annotation { "Feature Type Name" : "Feature", "Feature Type Description" : "" }
export const myFeature = defineFeature(function(context is Context, id is Id, definition is map)
    precondition{}
    {
        {
            var Q0;
            Q0=qCreatedBy(makeId("Top.planeOp"),FACE);
            var sketch = newSketch(context, id + "F0", { "sketchPlane" : qUnion([Q0])});
            skLineSegment(sketch, "E0", {"start": v(0, 0) * mm, "end": v(0, 609.6) * mm});
            skLineSegment(sketch, "E1", {"start": v(0, 609.6) * mm, "end": v(2743.2, 3534.73) * mm});
            skLineSegment(sketch, "E2", {"start": v(2743.2, 3534.73) * mm, "end": v(8839.2, 5486.4) * mm});
            skLineSegment(sketch, "E3", {"start": v(8839.2, 5486.4) * mm, "end": v(13696.12, 3681.04) * mm});
            skLineSegment(sketch, "E4", {"start": v(13696.12, 3681.04) * mm, "end": v(15849.6, 1524) * mm});
            skLineSegment(sketch, "E5", {"start": v(15849.6, 1524) * mm, "end": v(15849.6, 0) * mm});
            skLineSegment(sketch, "E6", {"start": v(0, 0) * mm, "end": v(15849.6, 0) * mm});
            skLineSegment(sketch, "E7", {"start": v(8839.2, 5486.4) * mm, "end": v(8839.2, 0) * mm, "construction": true});
            skLineSegment(sketch, "E8.bottom", {"start": v(13696.12, 2438.4) * mm, "end": v(5181.6, 2438.4) * mm, "construction": true});
            skLineSegment(sketch, "E8.top", {"start": v(13696.12, 0) * mm, "end": v(5181.6, 0) * mm});
            skLineSegment(sketch, "E8.left", {"start": v(13696.12, 2438.4) * mm, "end": v(13696.12, 0) * mm, "construction": true});
            skLineSegment(sketch, "E8.right", {"start": v(5181.6, 2438.4) * mm, "end": v(5181.6, 0) * mm, "construction": true});
            skLineSegment(sketch, "E9.bottom", {"start": v(0, 0) * mm, "end": v(1524, 0) * mm});
            skLineSegment(sketch, "E9.top", {"start": v(0, 609.6) * mm, "end": v(1524, 609.6) * mm});
            skLineSegment(sketch, "E9.right", {"start": v(1524, 0) * mm, "end": v(1524, 609.6) * mm});
            skSolve(sketch);
        }
        {
            var Q0;
            Q0=qCreatedBy(makeId("Top.planeOp"),FACE);
            var sketch = newSketch(context, id + "F1", { "sketchPlane" : qUnion([Q0])});
            skCircle(sketch, "E10", {"center": v(1828.8, 762) * mm, "radius": 45.72 * mm});
            skCircle(sketch, "E11", {"center": v(0, 609.6) * mm, "radius": 45.72 * mm});
            skCircle(sketch, "E12", {"center": v(5181.6, 2438.4) * mm, "radius": 45.72 * mm});
            skCircle(sketch, "E13", {"center": v(7924.8, 0) * mm, "radius": 45.72 * mm});
            skPoint(sketch, "E14.0", {"position": v(13696.12, 2438.4) * mm});
            skLineSegment(sketch, "E15.0", {"start": v(13696.12, 2438.4) * mm, "end": v(13696.12, 0) * mm});
            skCircle(sketch, "E16", {"center": v(13696.12, 3048) * mm, "radius": 45.72 * mm});
            skPoint(sketch, "E17.0", {"position": v(8839.2, 5486.4) * mm});
            skPoint(sketch, "E18.0", {"position": v(13696.12, 3681.04) * mm});
            skPoint(sketch, "E19.0", {"position": v(2743.2, 3534.73) * mm});
            skCircle(sketch, "E20", {"center": v(8839.2, 5486.4) * mm, "radius": 15.24 * mm});
            skCircle(sketch, "E21", {"center": v(2743.2, 3534.73) * mm, "radius": 15.24 * mm});
            skCircle(sketch, "E22", {"center": v(13696.12, 3681.04) * mm, "radius": 15.24 * mm});
            skLineSegment(sketch, "E23", {"start": v(13696.12, 2438.4) * mm, "end": v(13696.12, 3264.57) * mm, "construction": true});
            skSolve(sketch);
        }
        {
            var Q0;
            Q0=makeQuery(id+"F1.imprint","IMPRINT",FACE,{"disambiguationData":[TD([[makeQuery(id+"F1.imprint","IMPRINT",EDGE,{"derivedFrom":sQuery(id+"F1.wireOp",EDGE,"E11")}),1.0]])]});
            extrude(context, id + "F2", {"entities" : qUnion([Q0]), "depth" : 152.4 * mm, "offsetDistance" : 30.48 * mm});
        }
        {
            var Q0;
            Q0=makeQuery(id+"F1.imprint","IMPRINT",FACE,{"disambiguationData":[TD([[makeQuery(id+"F1.imprint","IMPRINT",EDGE,{"derivedFrom":sQuery(id+"F1.wireOp",EDGE,"E12")}),1.0]])]});
            extrude(context, id + "F3", {"entities" : qUnion([Q0]), "depth" : 2438.4 * mm, "offsetDistance" : 30.48 * mm});
        }
        {
            var Q0;
            Q0=makeQuery(id+"F1.imprint","IMPRINT",FACE,{"disambiguationData":[TD([[makeQuery(id+"F1.imprint","IMPRINT",EDGE,{"derivedFrom":sQuery(id+"F1.wireOp",EDGE,"E13")}),1.0]])]});
            extrude(context, id + "F4", {"entities" : qUnion([Q0]), "depth" : 6096 * mm, "offsetDistance" : 30.48 * mm});
        }
        {
            var Q0;
            Q0=makeQuery(id+"F1.imprint","IMPRINT",FACE,{"disambiguationData":[TD([[makeQuery(id+"F1.imprint","IMPRINT",EDGE,{"derivedFrom":sQuery(id+"F1.wireOp",EDGE,"E16")}),1.0]])]});
            var Q1;
            Q1=sQuery(id+"F1.wireOp",EDGE,"E16");
            extrude(context, id + "F5", {"entities" : qUnion([Q0]), "surfaceEntities" : qUnion([Q1]), "depth" : 3657.6 * mm, "offsetDistance" : 30.48 * mm});
        }
        {
            var Q0;
            Q0=makeQuery(id+"F1.imprint","IMPRINT",FACE,{"disambiguationData":[TD([[makeQuery(id+"F1.imprint","IMPRINT",EDGE,{"derivedFrom":sQuery(id+"F1.wireOp",EDGE,"E10")}),1.0]])]});
            extrude(context, id + "F6", {"entities" : qUnion([Q0]), "depth" : 1219.2 * mm, "offsetDistance" : 30.48 * mm});
        }
        {
            var Q0;
            Q0=makeQuery(id+"F2.opExtrude","CAP_FACE",FACE,{"disambiguationData":[OSD([sQuery(id+"F1.wireOp",EDGE,"E11")])],"isStart":false});
            var sketch = newSketch(context, id + "F7", { "sketchPlane" : qUnion([Q0])});
            skPoint(sketch, "E24.0", {"position": v(0, 609.6) * mm});
            skSolve(sketch);
        }
        {
            var Q0;
            Q0=makeQuery(id+"F6.opExtrude","CAP_FACE",FACE,{"disambiguationData":[OSD([sQuery(id+"F1.wireOp",EDGE,"E10")])],"isStart":false});
            var sketch = newSketch(context, id + "F8", { "sketchPlane" : qUnion([Q0])});
            skPoint(sketch, "E25.0", {"position": v(1828.8, 762) * mm});
            skSolve(sketch);
        }
        {
            var Q0;
            Q0=makeQuery(id+"F3.opExtrude","CAP_FACE",FACE,{"disambiguationData":[OSD([sQuery(id+"F1.wireOp",EDGE,"E12")])],"isStart":false});
            var sketch = newSketch(context, id + "F9", { "sketchPlane" : qUnion([Q0])});
            skPoint(sketch, "E26.0", {"position": v(5181.6, 2438.4) * mm});
            skSolve(sketch);
        }
        {
            var Q0;
            Q0=makeQuery(id+"F4.opExtrude","CAP_FACE",FACE,{"disambiguationData":[OSD([sQuery(id+"F1.wireOp",EDGE,"E13")])],"isStart":false});
            var sketch = newSketch(context, id + "F10", { "sketchPlane" : qUnion([Q0])});
            skPoint(sketch, "E27.0", {"position": v(7924.8, 0) * mm});
            skSolve(sketch);
        }
        {
            var Q0;
            Q0=makeQuery(id+"F5.opExtrude","CAP_FACE",FACE,{"disambiguationData":[OSD([sQuery(id+"F1.wireOp",EDGE,"E16")])],"isStart":false});
            var sketch = newSketch(context, id + "F11", { "sketchPlane" : qUnion([Q0])});
            skPoint(sketch, "E28.0", {"position": v(13696.12, 3048) * mm});
            skSolve(sketch);
        }
        {
            var Q0;
            Q0=qCreatedBy(makeId("Front.planeOp"),FACE);
            var sketch = newSketch(context, id + "F12", { "sketchPlane" : qUnion([Q0])});
            skPoint(sketch, "E29.0", {"position": v(0, 152.4) * mm});
            skPoint(sketch, "E30.0", {"position": v(1828.8, 1219.2) * mm});
            skPoint(sketch, "E31.0", {"position": v(5181.6, 2438.4) * mm});
            skPoint(sketch, "E32.0", {"position": v(7924.8, 6096) * mm});
            skPoint(sketch, "E33.0", {"position": v(13696.12, 3657.6) * mm});
            skPoint(sketch, "E34.0", {"position": v(15849.6, 0) * mm});
            skLineSegment(sketch, "E35", {"start": v(0, 152.4) * mm, "end": v(1828.8, 1219.2) * mm});
            skLineSegment(sketch, "E36", {"start": v(1828.8, 1219.2) * mm, "end": v(5181.6, 2438.4) * mm});
            skLineSegment(sketch, "E37", {"start": v(5181.6, 2438.4) * mm, "end": v(7924.8, 6096) * mm});
            skLineSegment(sketch, "E38", {"start": v(7924.8, 6096) * mm, "end": v(13696.12, 3657.6) * mm});
            skLineSegment(sketch, "E39", {"start": v(13696.12, 3657.6) * mm, "end": v(15849.6, 0) * mm});
            skLineSegment(sketch, "E40", {"start": v(0, 152.4) * mm, "end": v(0, 0) * mm});
            skLineSegment(sketch, "E41", {"start": v(0, 0) * mm, "end": v(15849.6, 0) * mm});
            skSolve(sketch);
        }
        {
            var Q0;
            Q0=sQuery(id+"F12.wireOp",VERTEX,"E34.0");
            var Q1;
            Q1=sQuery(id+"F0.wireOp",EDGE,"E6");
            cPlane(context, id + "F13", {"entities" : qUnion([Q0, Q1]), "cplaneType" : CPlaneType.LINE_POINT, "offset" : 25.4 * mm, "width" : 152.4 * mm, "height" : 152.4 * mm});
        }
        {
            var Q0;
            Q0=sQuery(id+"F0.wireOp",VERTEX,"E8.top.start");
            var Q1;
            Q1=sQuery(id+"F0.wireOp",EDGE,"E8.top");
            cPlane(context, id + "F14", {"entities" : qUnion([Q0, Q1]), "cplaneType" : CPlaneType.LINE_POINT, "offset" : 25.4 * mm, "width" : 152.4 * mm, "height" : 152.4 * mm});
        }
        {
            var Q0;
            Q0=sQuery(id+"F0.wireOp",VERTEX,"E7.end");
            var Q1;
            Q1=sQuery(id+"F0.wireOp",EDGE,"E8.top");
            cPlane(context, id + "F15", {"entities" : qUnion([Q0, Q1]), "cplaneType" : CPlaneType.LINE_POINT, "offset" : 25.4 * mm, "width" : 152.4 * mm, "height" : 152.4 * mm});
        }
        {
            var Q0;
            Q0=sQuery(id+"F1.wireOp",VERTEX,"E13.center");
            var Q1;
            Q1=sQuery(id+"F0.wireOp",EDGE,"E8.top");
            cPlane(context, id + "F16", {"entities" : qUnion([Q0, Q1]), "cplaneType" : CPlaneType.LINE_POINT, "offset" : 25.4 * mm, "width" : 152.4 * mm, "height" : 152.4 * mm});
        }
        {
            var Q0;
            Q0=sQuery(id+"F0.wireOp",VERTEX,"E8.top.end");
            var Q1;
            Q1=sQuery(id+"F0.wireOp",EDGE,"E6");
            cPlane(context, id + "F17", {"entities" : qUnion([Q0, Q1]), "cplaneType" : CPlaneType.LINE_POINT, "offset" : 25.4 * mm, "width" : 152.4 * mm, "height" : 152.4 * mm});
        }
        {
            var Q0;
            Q0=sQuery(id+"F1.wireOp",VERTEX,"E10.center");
            var Q1;
            Q1=sQuery(id+"F0.wireOp",EDGE,"E9.top");
            cPlane(context, id + "F18", {"entities" : qUnion([Q0, Q1]), "cplaneType" : CPlaneType.LINE_POINT, "offset" : 25.4 * mm, "width" : 152.4 * mm, "height" : 152.4 * mm});
        }
        {
            var Q0;
            Q0=qCreatedBy(id+"F13.planeOp",FACE);
            var sketch = newSketch(context, id + "F19", { "sketchPlane" : qUnion([Q0])});
            skPoint(sketch, "E42.0", {"position": v(1524, 0) * mm});
            skPoint(sketch, "E43.0", {"position": v(0, 0) * mm});
            skLineSegment(sketch, "E44", {"start": v(0, 0) * mm, "end": v(1524, 0) * mm});
            skSolve(sketch);
        }
        {
            var Q0;
            Q0=qCreatedBy(id+"F14.planeOp",FACE);
            var sketch = newSketch(context, id + "F20", { "sketchPlane" : qUnion([Q0])});
            skPoint(sketch, "E45.0", {"position": v(0, 3657.6) * mm});
            skPoint(sketch, "E46.0", {"position": v(-3681.04, 0) * mm});
            skFitSpline(sketch, "E47", {"points": [v(0, 3657.6) * mm, v(-2829.93, 3657.6) * mm, v(-3266.02, 3355.39) * mm, v(-3455.52, 2857.54) * mm, v(-3466.42, 2011.87) * mm, v(-3681.04, 0) * mm], "startDerivative": vector(-11892.45, -467.18) * mm, "endDerivative": vector(-448.43, -6710.95) * mm});
            skSolve(sketch);
        }
        {
            var Q0;
            Q0=qCreatedBy(id+"F15.planeOp",FACE);
            var sketch = newSketch(context, id + "F21", { "sketchPlane" : qUnion([Q0])});
            skPoint(sketch, "E48.0", {"position": v(-5486.4, 0) * mm});
            skPoint(sketch, "E49.0", {"position": v(-3048, 3657.6) * mm});
            skPoint(sketch, "E50", {"position": v(0, 5709.66) * mm});
            skFitSpline(sketch, "E51", {"points": [v(0, 5709.66) * mm, v(-1542.44, 4811.64) * mm, v(-3048, 3657.6) * mm, v(-5486.4, 0) * mm], "startDerivative": vector(-5647.14, -3250.63) * mm, "endDerivative": vector(-5724.6, -9712.29) * mm});
            skSolve(sketch);
        }
        {
            var Q0;
            Q0=qCreatedBy(id+"F16.planeOp",FACE);
            var sketch = newSketch(context, id + "F22", { "sketchPlane" : qUnion([Q0])});
            skPoint(sketch, "E52.0", {"position": v(0, 6096) * mm});
            skPoint(sketch, "E53", {"position": v(-5193.65, 0) * mm});
            skFitSpline(sketch, "E54", {"points": [v(0, 6096) * mm, v(-1926, 4551.62) * mm, v(-3350.94, 3287.9) * mm, v(-4609.72, 1384.51) * mm, v(-5193.65, 0) * mm], "startDerivative": vector(-7241.61, -5856.52) * mm, "endDerivative": vector(-2275.9, -6106.6) * mm});
            skSolve(sketch);
        }
        {
            var Q0;
            Q0=qCreatedBy(id+"F17.planeOp",FACE);
            var sketch = newSketch(context, id + "F23", { "sketchPlane" : qUnion([Q0])});
            skPoint(sketch, "E55.0", {"position": v(2438.4, 2438.4) * mm});
            skPoint(sketch, "E56.0", {"position": v(0, 2438.4) * mm});
            skPoint(sketch, "E57", {"position": v(4315.4, 0) * mm});
            skFitSpline(sketch, "E58", {"points": [v(0, 2438.4) * mm, v(1379.95, 2438.4) * mm, v(2438.4, 2438.4) * mm, v(3673.67, 1296.18) * mm, v(4315.4, 0) * mm], "startDerivative": vector(8349.63, -169.14) * mm, "endDerivative": vector(2877.01, -3268.1) * mm});
            skSolve(sketch);
        }
        {
            var Q0;
            Q0=qCreatedBy(makeId("Right.planeOp"),FACE);
            var Q1;
            Q1=sQuery(id+"F1.wireOp",VERTEX,"E19.0");
            cPlane(context, id + "F24", {"entities" : qUnion([Q0, Q1]), "cplaneType" : CPlaneType.PLANE_POINT, "offset" : 25.4 * mm, "width" : 152.4 * mm, "height" : 152.4 * mm});
        }
        {
            var Q0;
            Q0=qCreatedBy(id+"F24.planeOp",FACE);
            var sketch = newSketch(context, id + "F25", { "sketchPlane" : qUnion([Q0])});
            skPoint(sketch, "E59.0", {"position": v(3534.73, 0) * mm});
            skPoint(sketch, "E60", {"position": v(0, 1551.7) * mm});
            skFitSpline(sketch, "E61", {"points": [v(0, 1551.7) * mm, v(2052.91, 912.19) * mm, v(3534.73, 0) * mm], "startDerivative": vector(4102.53, -1027.58) * mm, "endDerivative": vector(2946.55, -2094.64) * mm});
            skSolve(sketch);
        }
        {
            var Q0;
            Q0=qCreatedBy(id+"F18.planeOp",FACE);
            var sketch = newSketch(context, id + "F26", { "sketchPlane" : qUnion([Q0])});
            skPoint(sketch, "E62.0", {"position": v(762, 1219.2) * mm});
            skPoint(sketch, "E63.0", {"position": v(0, 1219.2) * mm});
            skPoint(sketch, "E64", {"position": v(2559.69, 0) * mm});
            skFitSpline(sketch, "E65", {"points": [v(0, 1219.2) * mm, v(459.95, 1299.1) * mm, v(762, 1219.2) * mm, v(1566.31, 756.2) * mm, v(2559.69, 0) * mm], "startDerivative": vector(2615.98, 1638.56) * mm, "endDerivative": vector(1566.62, -2609.05) * mm});
            skSolve(sketch);
        }
        {
            var Q0;
            Q0=sQuery(id+"F0.wireOp",EDGE,"E0");
            var Q1;
            Q1=sQuery(id+"F26.wireOp",EDGE,"E65");
            var Q2;
            Q2=sQuery(id+"F25.wireOp",EDGE,"E61");
            var Q3;
            Q3=sQuery(id+"F23.wireOp",EDGE,"E58");
            var Q4;
            Q4=sQuery(id+"F22.wireOp",EDGE,"E54");
            var Q5;
            Q5=sQuery(id+"F21.wireOp",EDGE,"E51");
            var Q6;
            Q6=sQuery(id+"F20.wireOp",EDGE,"E47");
            var Q7;
            Q7=sQuery(id+"F0.wireOp",EDGE,"E5");
            loft(context, id + "F27", {"bodyType" : ToolBodyType.SURFACE, "wireProfilesArray" : [{ "wireProfileEntities" : qUnion([Q0]) }, { "wireProfileEntities" : qUnion([Q1]) }, { "wireProfileEntities" : qUnion([Q2]) }, { "wireProfileEntities" : qUnion([Q3]) }, { "wireProfileEntities" : qUnion([Q4]) }, { "wireProfileEntities" : qUnion([Q5]) }, { "wireProfileEntities" : qUnion([Q6]) }, { "wireProfileEntities" : qUnion([Q7]) }]});
        }
        {
            var Q0;
            Q0=makeQuery(id+"F0.imprint","IMPRINT",FACE,{"disambiguationData":[TD([[makeQuery(id+"F0.imprint","IMPRINT",EDGE,{"derivedFrom":sQuery(id+"F0.wireOp",EDGE,"E1")}),-1.0]])]});
            var sketch = newSketch(context, id + "F28", { "sketchPlane" : qUnion([Q0])});
            skPoint(sketch, "E66.0", {"position": v(0, 0) * mm});
            skPoint(sketch, "E67.0", {"position": v(15849.6, 0) * mm});
            skLineSegment(sketch, "E68.bottom", {"start": v(15849.6, 0) * mm, "end": v(0, 0) * mm});
            skLineSegment(sketch, "E68.top", {"start": v(15849.6, 5905.95) * mm, "end": v(0, 5905.95) * mm});
            skLineSegment(sketch, "E68.left", {"start": v(15849.6, 0) * mm, "end": v(15849.6, 5905.95) * mm});
            skLineSegment(sketch, "E68.right", {"start": v(0, 0) * mm, "end": v(0, 5905.95) * mm});
            skSolve(sketch);
        }
        {
            var Q0;
            {var subQ2=sQuery(id+"F28.wireOp",EDGE,"E68.top");Q0=makeQuery(id+"F28.imprint","IMPRINT",FACE,{"disambiguationData":[TD([[makeQuery(id+"F28.imprint","IMPRINT",EDGE,{"derivedFrom":subQ2}),1.0]])]});}
            var Q1;
            Q1=makeQuery(id+"F28.imprint","IMPRINT",FACE,{"disambiguationData":[TD([[makeQuery(id+"F28.imprint","IMPRINT",EDGE,{"derivedFrom":makeQuery(id+"F0.imprint","IMPRINT",EDGE,{"derivedFrom":sQuery(id+"F0.wireOp",EDGE,"E1")})}),-1.0]])]});
            var Q2;
            {var subQ4=makeQuery(id+"F0.imprint","IMPRINT",EDGE,{"derivedFrom":sQuery(id+"F0.wireOp",EDGE,"E9.top")});Q2=makeQuery(id+"F28.imprint","IMPRINT",FACE,{"disambiguationData":[TD([[makeQuery(id+"F28.imprint","IMPRINT",EDGE,{"derivedFrom":subQ4}),-1.0]])]});}
            extrude(context, id + "F29", {"entities" : qUnion([Q0, Q1, Q2]), "endBound" : BoundingType.UP_TO_NEXT, "depth" : 30.48 * mm, "offsetDistance" : 30.48 * mm});
        }
        {
            var Q0;
            Q0=makeQuery(id+"F29.opExtrude","SWEPT_FACE",FACE,{"disambiguationData":[OSD([sQuery(id+"F28.wireOp",EDGE,"E68.bottom")])]});
            var sketch = newSketch(context, id + "F30", { "sketchPlane" : qUnion([Q0])});
            skLineSegment(sketch, "E69.0", {"start": v(0, 0) * mm, "end": v(15849.6, 0) * mm});
            skFitSpline(sketch, "E70", {"points": [v(151.1, 0) * mm, v(1335.62, 1106.36) * mm, v(2951.57, 1454.2) * mm, v(5261.09, 1746.55) * mm, v(7429.78, 3342.38) * mm, v(9571.19, 3847.04) * mm, v(12476.41, 3315.1) * mm, v(14290.47, 1473.76) * mm, v(15422.56, 0) * mm], "startDerivative": vector(8330.38, 16085.02) * mm, "endDerivative": vector(9379.69, -12005.89) * mm});
            skSolve(sketch);
        }
        {
            var Q0;
            {var subQ0=sQuery(id+"F30.wireOp",EDGE,"E70");Q0=makeQuery(id+"F30.imprint","IMPRINT",FACE,{"disambiguationData":[TD([[makeQuery(id+"F30.imprint","IMPRINT",EDGE,{"derivedFrom":subQ0}),-1.0]])]});}
            var Q1;
            Q1=sQuery(id+"F30.wireOp",EDGE,"E69.0");
            revolve(context, id + "F31", {"operationType" : NewBodyOperationType.REMOVE, "surfaceOperationType" : NewSurfaceOperationType.NEW, "entities" : qUnion([Q0]), "axis" : qUnion([Q1]), "revolveType" : RevolveType.FULL, "oppositeDirection" : true});
        }
        {
            var Q0;
            Q0=makeQuery(id+"F0.imprint","IMPRINT",FACE,{"disambiguationData":[TD([[makeQuery(id+"F0.imprint","IMPRINT",EDGE,{"derivedFrom":sQuery(id+"F0.wireOp",EDGE,"E1")}),-1.0]])]});
            var sketch = newSketch(context, id + "F32", { "sketchPlane" : qUnion([Q0])});
            skLineSegment(sketch, "E71.0", {"start": v(0, 0) * mm, "end": v(15849.6, 0) * mm});
            skFitSpline(sketch, "E72", {"points": [v(0, 598.51) * mm, v(834.4, 733.54) * mm, v(1886.87, 662) * mm, v(2862.7, 805.06) * mm, v(3956.04, 0) * mm], "startDerivative": vector(3191.49, 470.09) * mm, "endDerivative": vector(434.84, -6732.44) * mm});
            skSolve(sketch);
        }
        {
            var Q0;
            {var subQ1=makeQuery(id+"F0.imprint","IMPRINT",EDGE,{"derivedFrom":sQuery(id+"F0.wireOp",EDGE,"E9.right")});Q0=makeQuery(id+"F32.imprint","IMPRINT",FACE,{"disambiguationData":[TD([[makeQuery(id+"F32.imprint","IMPRINT",EDGE,{"derivedFrom":subQ1}),-1.0]])]});}
            var Q1;
            Q1=makeQuery(id+"F0.imprint","IMPRINT",FACE,{"disambiguationData":[TD([[makeQuery(id+"F0.imprint","IMPRINT",EDGE,{"derivedFrom":sQuery(id+"F0.wireOp",EDGE,"E9.bottom")}),1.0]])]});
            extrude(context, id + "F33", {"entities" : qUnion([Q0, Q1]), "operationType" : NewBodyOperationType.REMOVE, "endBound" : BoundingType.THROUGH_ALL, "depth" : 30.48 * mm, "offsetDistance" : 30.48 * mm});
        }
        {
            var Q0;
            Q0=makeQuery(id+"F29.opExtrude","SWEPT_BODY",BODY,{"disambiguationData":[OSD([sQuery(id+"F28.wireOp",EDGE,"E68.bottom"),sQuery(id+"F28.wireOp",EDGE,"E68.top"),sQuery(id+"F28.wireOp",EDGE,"E68.left"),sQuery(id+"F28.wireOp",EDGE,"E68.right")])]});
            var Q1;
            Q1=qCreatedBy(makeId("Front.planeOp"),FACE);
            mirror(context, id + "F34", {"operationType" : NewBodyOperationType.ADD, "entities" : qUnion([Q0]), "mirrorPlane" : qUnion([Q1])});
        }
        {
            var Q0;
            Q0=makeQuery(id+"F3.opExtrude","SWEPT_BODY",BODY,{"disambiguationData":[OSD([sQuery(id+"F1.wireOp",EDGE,"E12")])]});
            var Q1;
            Q1=makeQuery(id+"F5.opExtrude","SWEPT_BODY",BODY,{"disambiguationData":[OSD([sQuery(id+"F1.wireOp",EDGE,"E16")])]});
            var Q2;
            Q2=makeQuery(id+"F6.opExtrude","SWEPT_BODY",BODY,{"disambiguationData":[OSD([sQuery(id+"F1.wireOp",EDGE,"E10")])]});
            var Q3;
            Q3=makeQuery(id+"F29.opExtrude","SWEPT_BODY",BODY,{"disambiguationData":[OSD([sQuery(id+"F28.wireOp",EDGE,"E68.bottom"),sQuery(id+"F28.wireOp",EDGE,"E68.top"),sQuery(id+"F28.wireOp",EDGE,"E68.left"),sQuery(id+"F28.wireOp",EDGE,"E68.right")])]});
            var Q4;
            Q4=qCreatedBy(makeId("Front.planeOp"),FACE);
            mirror(context, id + "F35", {"entities" : qUnion([Q0, Q1, Q2, Q3]), "mirrorPlane" : qUnion([Q4])});
        }
        {
            var Q0;
            Q0=qCreatedBy(makeId("Top.planeOp"),FACE);
            var sketch = newSketch(context, id + "F36", { "sketchPlane" : qUnion([Q0])});
            skLineSegment(sketch, "E73", {"start": v(133350.66, 124767.72) * mm, "end": v(173860.23, -195902.15) * mm});
            skSolve(sketch);
        }
        {
            var Q0;
            Q0=qCreatedBy(makeId("Right.planeOp"),FACE);
            var sketch = newSketch(context, id + "F37", { "sketchPlane" : qUnion([Q0])});
            skLineSegment(sketch, "E74.0", {"start": v(124767.72, 0) * mm, "end": v(-195902.15, 0) * mm});
            skSolve(sketch);
        }
        {
            var Q0;
            Q0 = qSketchRegion(id + "F37", true);
            var Q1;
            Q1=sQuery(id+"F37.wireOp",EDGE,"E74.0");
            extrude(context, id + "F38", {"entities" : qUnion([Q0]), "bodyType" : ToolBodyType.SURFACE, "surfaceEntities" : qUnion([Q1]), "depth" : 60960 * mm, "offsetDistance" : 30.48 * mm, "hasSecondDirection" : true, "secondDirectionOppositeDirection" : true, "secondDirectionDepth" : 60960 * mm});
        }
    });